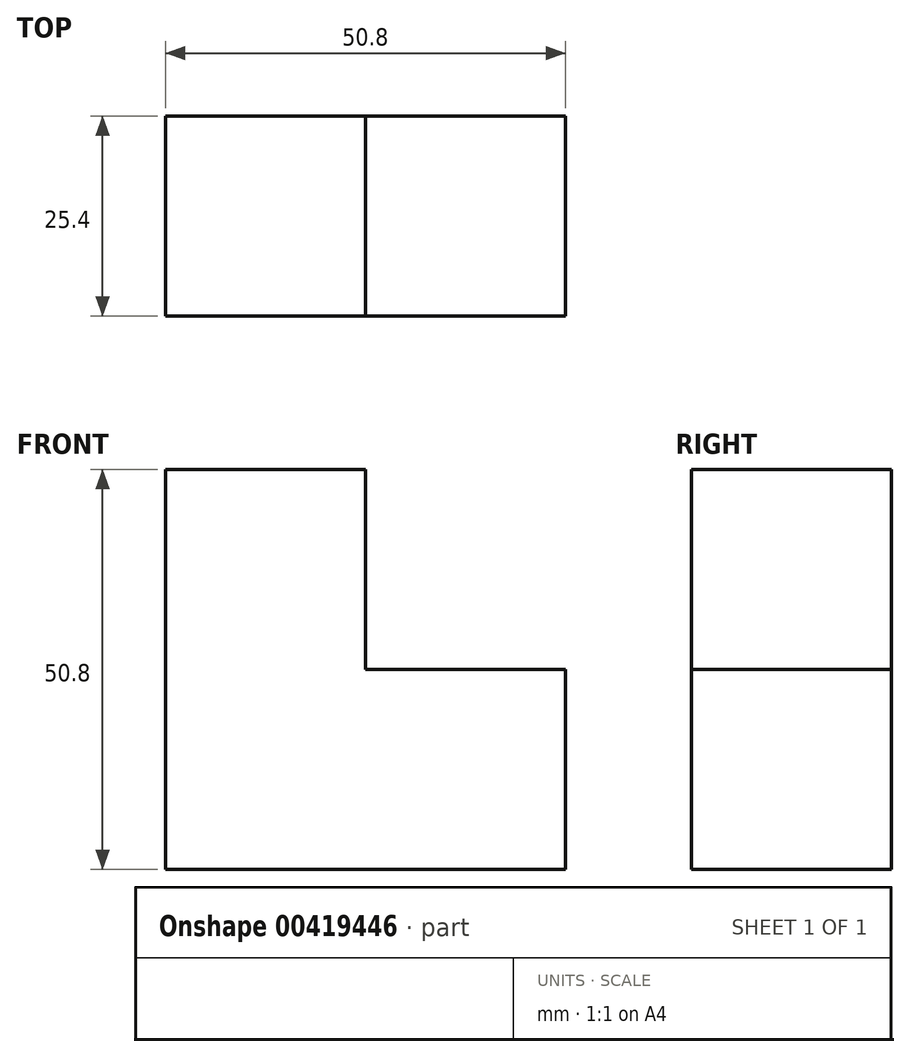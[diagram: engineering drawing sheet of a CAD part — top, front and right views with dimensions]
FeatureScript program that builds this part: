
annotation { "Feature Type Name" : "Feature", "Feature Type Description" : "" }
export const myFeature = defineFeature(function(context is Context, id is Id, definition is map)
    precondition{}
    {
        {
            var Q0;
            Q0=qCreatedBy(makeId("Front.planeOp"),FACE);
            var sketch = newSketch(context, id + "F0", { "sketchPlane" : qUnion([Q0])});
            skLineSegment(sketch, "E0", {"start": v(-55.43, 42.93) * mm, "end": v(-55.43, -7.87) * mm});
            skLineSegment(sketch, "E1", {"start": v(-55.43, -7.87) * mm, "end": v(-4.63, -7.87) * mm});
            skLineSegment(sketch, "E2", {"start": v(-55.43, 42.93) * mm, "end": v(-30.03, 42.93) * mm});
            skLineSegment(sketch, "E3", {"start": v(-30.03, 42.93) * mm, "end": v(-30.03, 17.53) * mm});
            skLineSegment(sketch, "E4", {"start": v(-30.03, 17.53) * mm, "end": v(-4.63, 17.53) * mm});
            skLineSegment(sketch, "E5", {"start": v(-4.63, 17.53) * mm, "end": v(-4.63, -7.87) * mm});
            skSolve(sketch);
        }
        {
            var Q0;
            Q0 = qSketchRegion(id + "F0", true);
            extrude(context, id + "F1", {"entities" : qUnion([Q0]), "depth" : 25.4 * mm, "offsetDistance" : 25.4 * mm});
        }
    });
